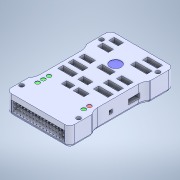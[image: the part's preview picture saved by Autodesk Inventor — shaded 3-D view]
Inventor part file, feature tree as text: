
AUTODESK INVENTOR PART (.ipt)
format: ipt  version: 2020 (Build 240168000, 168)  size: 848,384 bytes
history: mixed  units: in
note: dims shown in document units (in); Inventor stores cm internally (conversion verified against a paired STEP export)
features: chamfer x1, imported_body x1
ambient origin geometry x8: Origin, YZ Plane, XZ Plane, XY Plane, X Axis, Y Axis, Z Axis, Center Point
bodies: Solid1 (imported_parasolid)
feature tree (2):
  chamfer  "Chamfer1"  [1 undecoded]
  imported_body  NMx_Import_Brep_tag  [imported B-rep: ~15 faces, bbox_mm=[45.4406, 14.732, 34.769986]]
note: 1 required parameter value undecoded (feature->parameter linkage not recoverable at this tier; creation-order binding heuristic only, values carry confidence <= 0.55)
